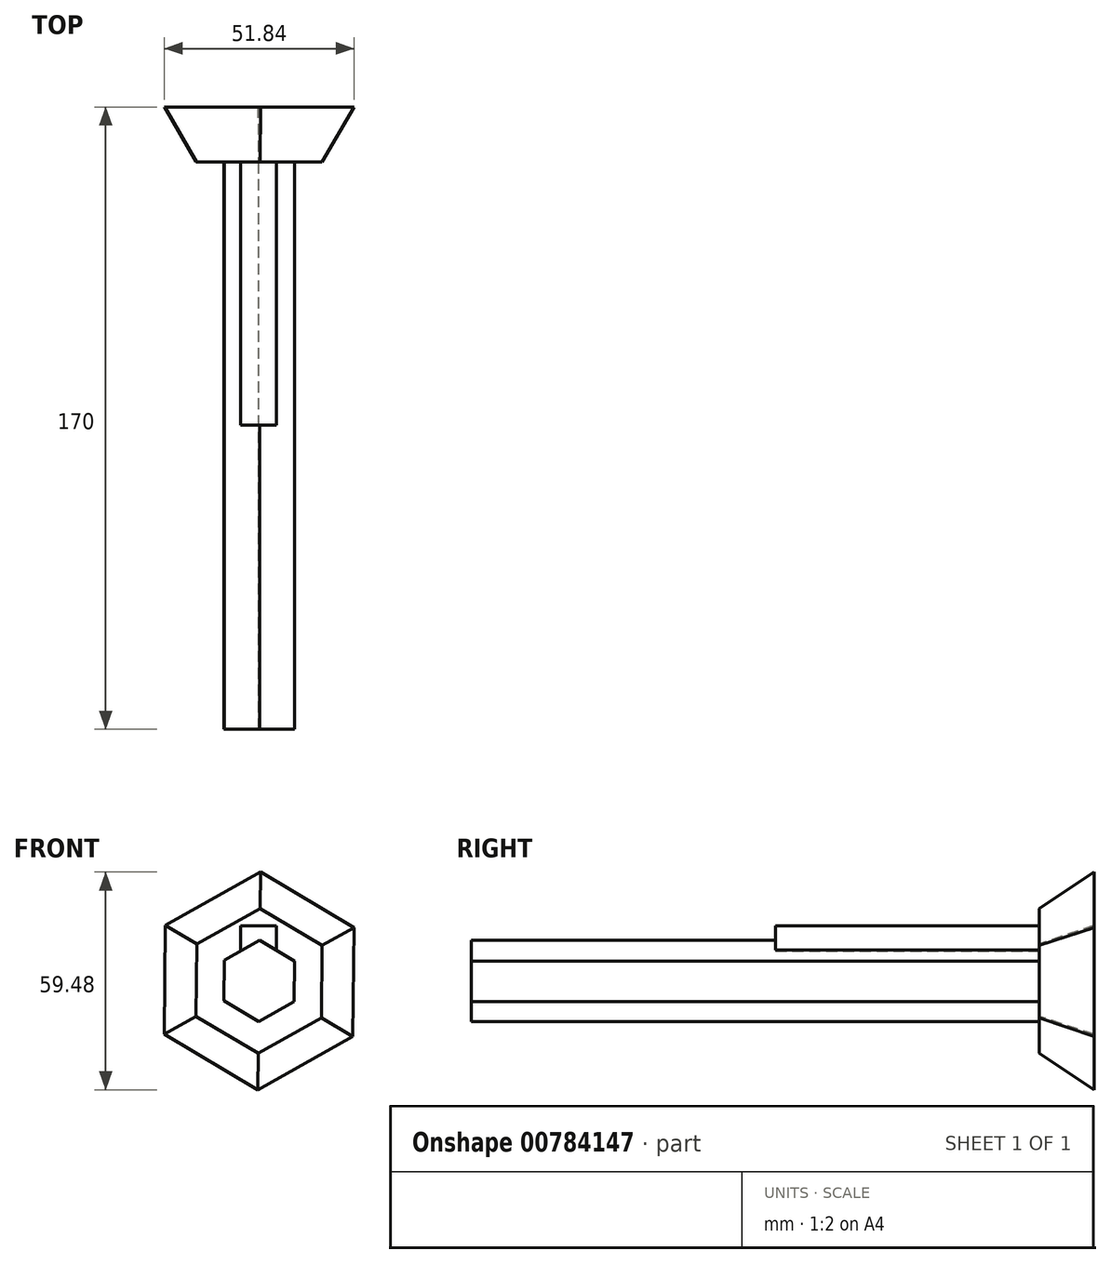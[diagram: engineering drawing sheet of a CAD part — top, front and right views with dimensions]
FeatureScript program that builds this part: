
annotation { "Feature Type Name" : "Feature", "Feature Type Description" : "" }
export const myFeature = defineFeature(function(context is Context, id is Id, definition is map)
    precondition{}
    {
        {
            var Q0;
            Q0=qCreatedBy(makeId("Front.planeOp"),FACE);
            var sketch = newSketch(context, id + "F0", { "sketchPlane" : qUnion([Q0])});
            skLineSegment(sketch, "E0.0", {"start": v(9.57, -5.67) * mm, "end": v(-0.13, -11.12) * mm});
            skLineSegment(sketch, "E0.1", {"start": v(-0.13, -11.12) * mm, "end": v(-9.7, -5.45) * mm});
            skLineSegment(sketch, "E0.2", {"start": v(-9.7, -5.45) * mm, "end": v(-9.57, 5.67) * mm});
            skLineSegment(sketch, "E0.3", {"start": v(-9.57, 5.67) * mm, "end": v(0.13, 11.12) * mm});
            skLineSegment(sketch, "E0.4", {"start": v(0.13, 11.12) * mm, "end": v(9.7, 5.45) * mm});
            skLineSegment(sketch, "E0.5", {"start": v(9.7, 5.45) * mm, "end": v(9.57, -5.67) * mm});
            skSolve(sketch);
        }
        {
            var Q0;
            Q0=makeQuery(id+"F0.imprint","IMPRINT",FACE,{"disambiguationData":[TD([[makeQuery(id+"F0.imprint","IMPRINT",EDGE,{"derivedFrom":sQuery(id+"F0.wireOp",EDGE,"E0.0")}),-1.0]])]});
            var Q1;
            Q1=sQuery(id+"F0.wireOp",EDGE,"E0.0");
            var Q2;
            Q2=sQuery(id+"F0.wireOp",EDGE,"E0.1");
            var Q3;
            Q3=sQuery(id+"F0.wireOp",EDGE,"E0.2");
            var Q4;
            Q4=sQuery(id+"F0.wireOp",EDGE,"E0.3");
            var Q5;
            Q5=sQuery(id+"F0.wireOp",EDGE,"E0.4");
            var Q6;
            Q6=sQuery(id+"F0.wireOp",EDGE,"E0.5");
            extrude(context, id + "F1", {"entities" : qUnion([Q0]), "surfaceEntities" : qUnion([Q1, Q2, Q3, Q4, Q5, Q6]), "depth" : 155 * mm, "offsetDistance" : 25 * mm, "symmetric" : true});
        }
        {
            var Q0;
            Q0=makeQuery(id+"F1.opExtrude","CAP_FACE",FACE,{"disambiguationData":[OSD([sQuery(id+"F0.wireOp",EDGE,"E0.0"),sQuery(id+"F0.wireOp",EDGE,"E0.1"),sQuery(id+"F0.wireOp",EDGE,"E0.2"),sQuery(id+"F0.wireOp",EDGE,"E0.3"),sQuery(id+"F0.wireOp",EDGE,"E0.4"),sQuery(id+"F0.wireOp",EDGE,"E0.5")])],"isStart":true});
            var sketch = newSketch(context, id + "F2", { "sketchPlane" : qUnion([Q0])});
            skCircle(sketch, "E1.cCircle", {"center": v(0, 0) * mm, "radius": 17.1 * mm, "construction": true});
            skLineSegment(sketch, "E1.0", {"start": v(17.2, -9.68) * mm, "end": v(0.22, -19.74) * mm});
            skLineSegment(sketch, "E1.1", {"start": v(0.22, -19.74) * mm, "end": v(-16.98, -10.06) * mm});
            skLineSegment(sketch, "E1.2", {"start": v(-16.98, -10.06) * mm, "end": v(-17.2, 9.68) * mm});
            skLineSegment(sketch, "E1.3", {"start": v(-17.2, 9.68) * mm, "end": v(-0.22, 19.74) * mm});
            skLineSegment(sketch, "E1.4", {"start": v(-0.22, 19.74) * mm, "end": v(16.98, 10.06) * mm});
            skLineSegment(sketch, "E1.5", {"start": v(16.98, 10.06) * mm, "end": v(17.2, -9.68) * mm});
            skPoint(sketch, "E1.0.midPoint", {"position": v(8.71, -14.7) * mm});
            skSolve(sketch);
        }
        {
            var Q0;
            Q0=makeQuery(id+"F2.imprint","IMPRINT",FACE,{"disambiguationData":[TD([[makeQuery(id+"F2.imprint","IMPRINT",EDGE,{"derivedFrom":sQuery(id+"F2.wireOp",EDGE,"E1.0")}),-1.0]])]});
            var Q1;
            Q1=makeQuery(id+"F2.imprint","IMPRINT",FACE,{"disambiguationData":[TD([[makeQuery(id+"F2.imprint","IMPRINT",EDGE,{"derivedFrom":makeQuery(id+"F1.opExtrude","CAP_EDGE",EDGE,{"disambiguationData":[OSD([sQuery(id+"F0.wireOp",EDGE,"E0.0")])],"isStart":true})}),1.0]])]});
            extrude(context, id + "F3", {"entities" : qUnion([Q0, Q1]), "operationType" : NewBodyOperationType.ADD, "depth" : 15 * mm, "offsetDistance" : 25 * mm, "hasDraft" : true, "draftAngle" : 30 * degree});
        }
        {
            var Q0;
            Q0=qCreatedBy(makeId("Top.planeOp"),FACE);
            var sketch = newSketch(context, id + "F4", { "sketchPlane" : qUnion([Q0])});
            skLineSegment(sketch, "E2.bottom", {"start": v(-5.02, 86.99) * mm, "end": v(4.7, 86.99) * mm});
            skLineSegment(sketch, "E2.top", {"start": v(-5.02, 5.6) * mm, "end": v(4.7, 5.6) * mm});
            skLineSegment(sketch, "E2.left", {"start": v(-5.02, 86.99) * mm, "end": v(-5.02, 5.6) * mm});
            skLineSegment(sketch, "E2.right", {"start": v(4.7, 86.99) * mm, "end": v(4.7, 5.6) * mm});
            skSolve(sketch);
        }
        {
            var Q0;
            Q0=qSketchRegion(id+"F4",true);
            extrude(context, id + "F5", {"entities" : qUnion([Q0]), "operationType" : NewBodyOperationType.ADD, "depth" : 15 * mm, "offsetDistance" : 25 * mm});
        }
    });
